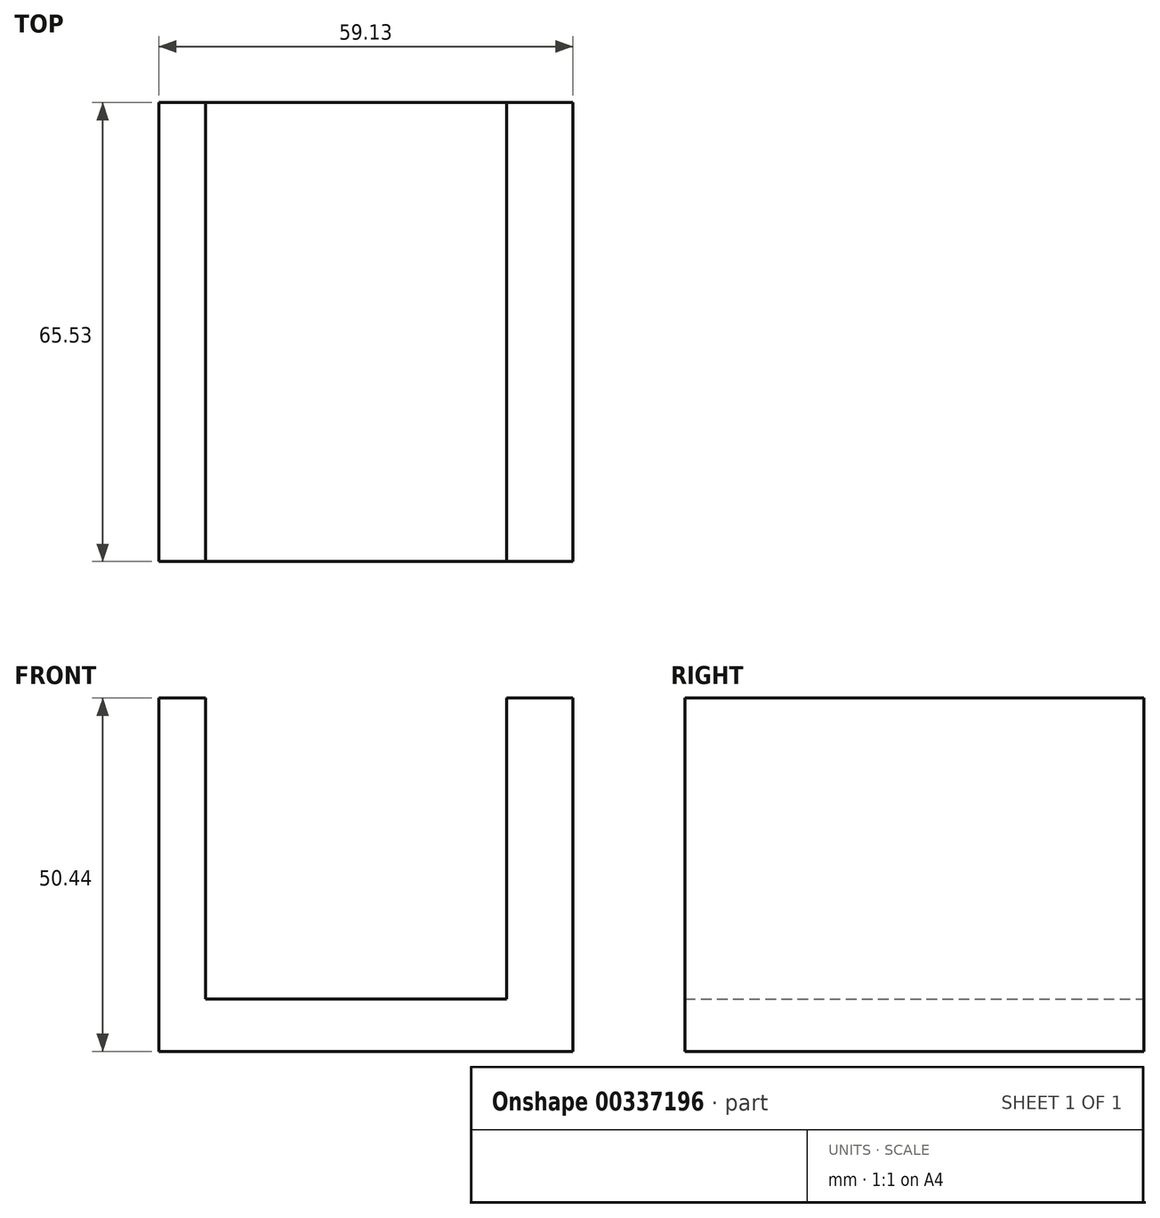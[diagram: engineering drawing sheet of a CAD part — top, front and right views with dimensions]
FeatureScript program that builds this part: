
annotation { "Feature Type Name" : "Feature", "Feature Type Description" : "" }
export const myFeature = defineFeature(function(context is Context, id is Id, definition is map)
    precondition{}
    {
        {
            var Q0;
            Q0=qCreatedBy(makeId("Front.planeOp"),FACE);
            var sketch = newSketch(context, id + "F0", { "sketchPlane" : qUnion([Q0])});
            skLineSegment(sketch, "E0", {"start": v(-59.13, 50.44) * mm, "end": v(-59.13, 0) * mm});
            skLineSegment(sketch, "E1", {"start": v(-59.13, 0) * mm, "end": v(0, 0) * mm});
            skLineSegment(sketch, "E2", {"start": v(0, 0) * mm, "end": v(0, 50.44) * mm});
            skLineSegment(sketch, "E3", {"start": v(0, 50.44) * mm, "end": v(-9.45, 50.44) * mm});
            skLineSegment(sketch, "E4", {"start": v(-9.45, 50.44) * mm, "end": v(-9.45, 7.47) * mm});
            skLineSegment(sketch, "E5", {"start": v(-9.45, 7.47) * mm, "end": v(-52.43, 7.47) * mm});
            skLineSegment(sketch, "E6", {"start": v(-52.43, 7.47) * mm, "end": v(-52.43, 50.44) * mm});
            skLineSegment(sketch, "E7", {"start": v(-52.43, 50.44) * mm, "end": v(-59.13, 50.44) * mm});
            skSolve(sketch);
        }
        {
            var Q0;
            Q0 = qSketchRegion(id + "F0", true);
            var Q1;
            Q1 = qSketchRegion(id + "F2", true);
            extrude(context, id + "F1", {"entities" : qUnion([Q0, Q1]), "depth" : 65.53 * mm});
        }
    });
